# Revit family: 0052852 Feilo Sylvania Lighting Fixture IVY 2 LED 600X600 43W 4000K EB UGR19
name_source: partatom
category: Lighting Fixtures
revit_build: Autodesk Revit 2017 (Build: 20190507_1515(x64)
units: mm (PartAtom-declared; Revit-internal decimal feet)

## family parameters
Cut with Voids When Loaded = No
Host = Face
Light Source = Yes
OmniClass Number = 23.80.70.11.17
OmniClass Title = Specialized Lighting by Location or Use
Part Type = Normal
Room Calculation Point = No
Round Connector Dimension = Use Diameter
Shared = No

## types (1)
- 0052852 IVY 2 LED 600X600 43W 4000K EB UGR19
    Apparent Load = 43 VA
    Assembly Code = D5020200
    AssetType = Fixed
    Color Filter = 16777215
    Default Elevation = 0 mm  [stored 0 ft]
    Description = Recessed 600mm x 600mm, lay-in, UGR<19 LED luminaire, 4000K Neutral White, Non-dimmable, 4082lm, 43W, 50,000 hours, Glow Wire Test 850°C
    Dimming Lamp Color Temperature Shift = <None>
    DimmingControlOptions = Non dimmable
    DocumentationLiterature = http://www.sylvania-lighting.com
    DurationUnit = hours
    ElectricShockClassification = Class I
    Emit Shape Visible in Rendering = No
    Emit from Rectangle Length = 558 mm  [stored 1.83071 ft]
    Emit from Rectangle Width = 558 mm  [stored 1.83071 ft]
    ExpectedLife = 50000
    IfcExportAs = IfcLightFixtureType
    IfcExportType = IfcLightFixtureType
    ImpactProtectionIndex = IK02
    IngressProtection = IP20
    Inner Length_old = 574 mm
    Inner Width_old = 574 mm
    InputVoltage = 220-240V~
    Keynote = 16500
    Lamp = LED
    LampColourRenderingIndex = 0
    LampColourTemperature = 4000 K
    LampNominalLuminous = 4082 lm
    LampsType = LED
    LightOutputRatio = 100
    LuminousEfficacy = 94.93 lm/W
    Manufacturer = Feilo Sylvania
    ManufacturerName = Feilo Sylvania
    Material = powder coated steel + aluminium housing, polycarbonate diffuser
    Material_1_FEILO = Aluminum_Sylvania_Ivy 2 LED_White 9016
    Material_2_FEILO = Aluminum_Sylvania_Ivy 2 LED_White
    Material_3_FEILO = Acrylic_Sylvania_Ivy 2 LED_White_Translucent
    Material_4_FEILO = <By Category>
    Model = IVY 2 LED 600X600 43W 4000K EB UGR19
    ModelNumber = 0052852
    ModelReference = IVY 2 LED 600X600 43W 4000K EB UGR19
    Name = IVY 2 LED 600X600 43W 4000K EB UGR19
    NominalHeight = 52 mm
    NominalLength = 596 mm  [stored 1.95538 ft]
    NominalWidth = 0 mm  [stored 0 ft]
    Photometric Web File = 0052852.ies
    PowerConsumption = 43 W
    PowerFactor = 0
    Tilt Angle = -90.00°
    TypeName = IVY 2 LED 600X600 43W 4000K EB UGR19
    URL = http://www.sylvania-lighting.com
    Voltage = 230 V
    Weight = 3.582 kg

note: [stored X ft] marks values corroborated as IEEE doubles in the binary element streams (Revit-internal decimal feet)

## geometry (parser evidence)
native form markers: Sweep x4
no freeform markers — native parametric forms only
